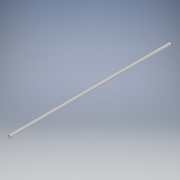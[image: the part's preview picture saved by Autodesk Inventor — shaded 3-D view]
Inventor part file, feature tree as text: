
AUTODESK INVENTOR PART (.ipt)
format: ipt  version: 2019 (Build 230136000, 136)  size: 89,600 bytes
history: native  units: mm
features: extrude x1, sketch x1
ambient origin geometry x8: Origin, YZ Plane, XZ Plane, XY Plane, X Axis, Y Axis, Z Axis, Center Point
bodies: Solid1 (feature_tree)
feature tree (2):
  extrude  "Extrusion1"  Depth=214.0mm TaperAngle=0.0deg
  sketch  "Sketch1"  dims[d0=3.2mm d1=214.0mm d2=0.0mm]
